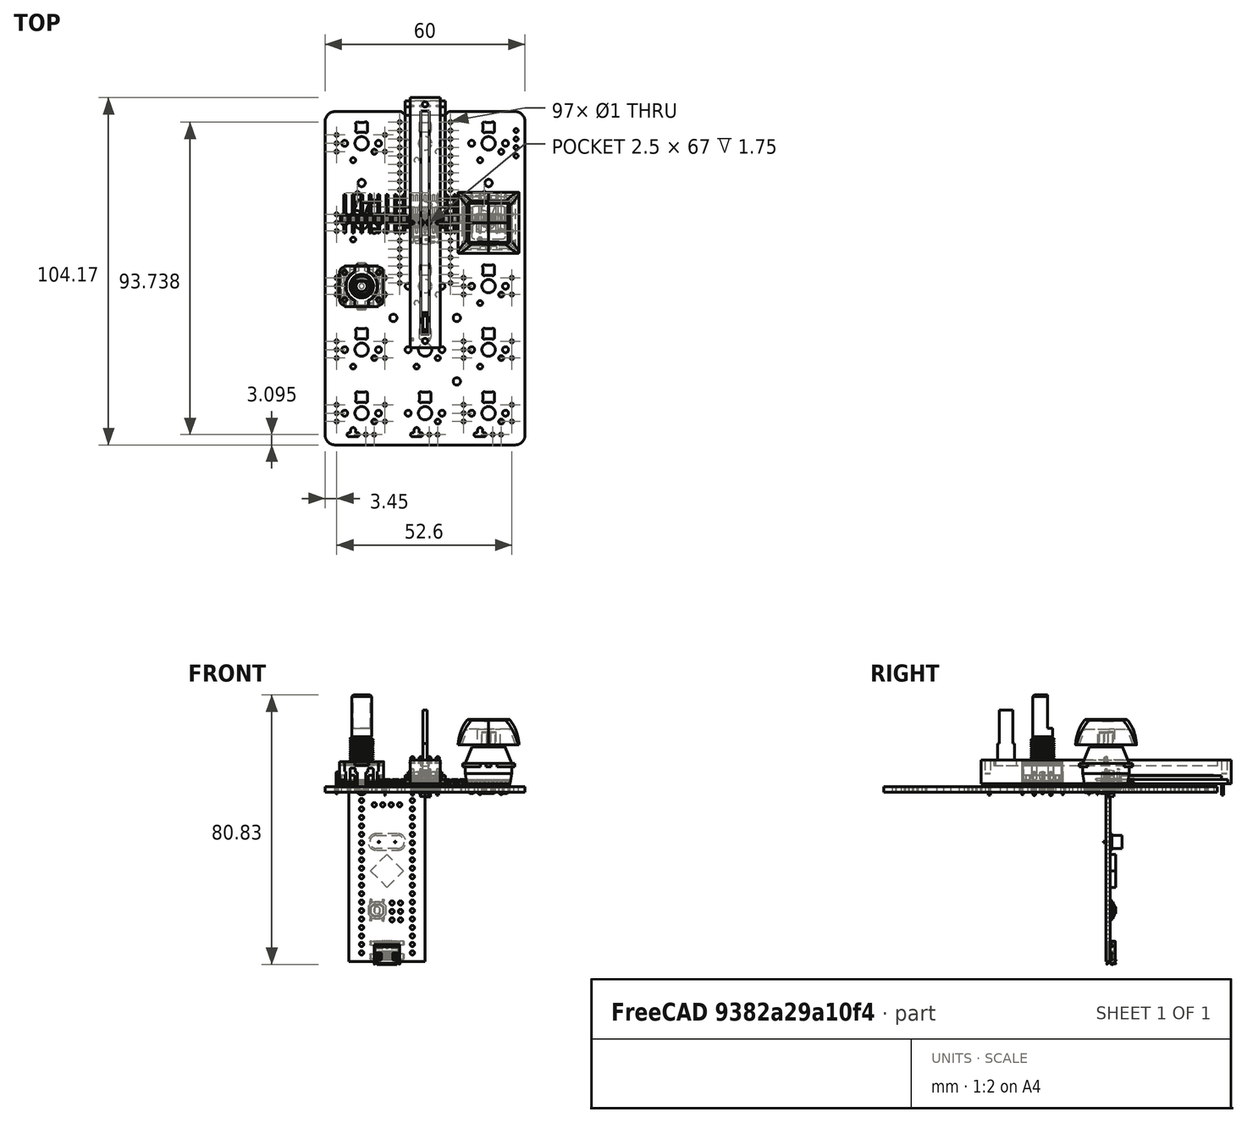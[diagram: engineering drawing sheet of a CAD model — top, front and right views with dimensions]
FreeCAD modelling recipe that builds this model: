
FCSTD DOCUMENT  (FreeCAD 2022.709R28846 (Git))
Label: keeby_cat_electronics_v1.0
License: All rights reserved
LicenseURL: http://en.wikipedia.org/wiki/All_rights_reserved
objects: Part::Feature×118, App::Link×53, Part::Compound2×10, App::Part×8, App::DocumentObjectGroup×3, PartDesign::CoordinateSystem×1, Sketcher::SketchObject×1
note: 120 computed .brp shape members not serialized (recipe doc carries the construction recipe); baked Part::Feature solids carry a one-line shape summary decoded from their .brp

FEATURE [PartDesign::CoordinateSystem] Local_CS_61fa
  AttacherType = Attacher::AttachEngine3D
  TreeRank = 3
FEATURE [Part::Feature] Pcb_61fa
  Placement = pos=(-92.16,90.4,-1) rot=(0,0,1;0rad)
  TreeRank = 4
  shape: bbox 60 x 100 x 1.6 mm, 469 faces (baked)
FEATURE [Sketcher::SketchObject] PCB_Sketch_61fa
  ArcFitTolerance = 0
  FullyConstrained = false
  TreeRank = 0
  sketch-geometry (16):
    g0: LineSegment StartX=-6.707 StartY=33.038 StartZ=0 EndX=-6.293 EndY=32.624 EndZ=0
    g1: LineSegment StartX=27 StartY=-66.669 StartZ=0 EndX=-27 EndY=-66.669 EndZ=0
    g2: LineSegment StartX=-27 StartY=33.331 StartZ=0 EndX=-7.414 EndY=33.331 EndZ=0
    g3: LineSegment StartX=-5.586 StartY=32.331 StartZ=0 EndX=5.586 EndY=32.331 EndZ=0
    g4: LineSegment StartX=7.414 StartY=33.331 StartZ=0 EndX=27 EndY=33.331 EndZ=0
    g5: LineSegment StartX=30 StartY=30.331 StartZ=0 EndX=30 EndY=-63.669 EndZ=0
    g6: LineSegment StartX=-30 StartY=-63.669 StartZ=0 EndX=-30 EndY=30.331 EndZ=0
    g7: LineSegment StartX=6.293 StartY=32.624 StartZ=0 EndX=6.707 EndY=33.038 EndZ=0
    g8: ArcOfCircle CenterX=-5.58541 CenterY=33.3319 CenterZ=0 NormalX=0 NormalY=0 NormalZ=-1 AngleXU=-1.57021 Radius=1.0009 StartAngle=0 EndAngle=0.784588
    g9: ArcOfCircle CenterX=-26.9989 CenterY=30.3299 CenterZ=0 NormalX=0 NormalY=0 NormalZ=-1 AngleXU=0.000364935 Radius=3.00109 StartAngle=6.28318 EndAngle=7.85325
    g10: ArcOfCircle CenterX=26.9989 CenterY=30.3299 CenterZ=0 NormalX=0 NormalY=0 NormalZ=-1 AngleXU=1.57116 Radius=3.00109 StartAngle=0 EndAngle=1.57007
    g11: ArcOfCircle CenterX=5.58549 CenterY=33.3317 CenterZ=0 NormalX=0 NormalY=0 NormalZ=-1 AngleXU=-2.35605 Radius=1.00072 StartAngle=0 EndAngle=0.784737
    g12: ArcOfCircle CenterX=-7.41449 CenterY=32.3303 CenterZ=0 NormalX=0 NormalY=0 NormalZ=-1 AngleXU=1.57129 Radius=1.00067 StartAngle=0 EndAngle=0.784782
    g13: ArcOfCircle CenterX=27.0006 CenterY=-63.6696 CenterZ=0 NormalX=0 NormalY=0 NormalZ=-1 AngleXU=3.14139 Radius=2.99938 StartAngle=0 EndAngle=1.57121
    g14: ArcOfCircle CenterX=7.4146 CenterY=32.3301 CenterZ=0 NormalX=0 NormalY=0 NormalZ=-1 AngleXU=0.785632 Radius=1.00093 StartAngle=0 EndAngle=0.784565
    g15: ArcOfCircle CenterX=-27.0006 CenterY=-63.6696 CenterZ=0 NormalX=0 NormalY=0 NormalZ=-1 AngleXU=-1.571 Radius=2.99938 StartAngle=0 EndAngle=1.57121
  constraints (16):
    c: Coincident(g6,g15)
    c: Coincident(g6,g9)
    c: Coincident(g1,g15)
    c: Coincident(g2,g9)
    c: Coincident(g2,g12)
    c: Coincident(g0,g12)
    c: Coincident(g0,g8)
    c: Coincident(g3,g8)
    c: Coincident(g3,g11)
    c: Coincident(g7,g11)
    c: Coincident(g7,g14)
    c: Coincident(g4,g14)
    c: Coincident(g1,g13)
    c: Coincident(g4,g10)
    c: Coincident(g5,g13)
    c: Coincident(g5,g10)
FEATURE [App::Part] Board_Geoms_61fa
  ClaimAllChildren = false
  ExportMode = 1
  Group = -> [Local_CS_61fa,Pcb_61fa,PCB_Sketch_61fa]
  Origin = -> Origin
  Placement = pos=(0,0,2) rot=(0,0,1;0rad)
  TreeRank = 5
  _ExportChildren = -> [Local_CS_61fa,Pcb_61fa,PCB_Sketch_61fa]
  _GroupVersion = 1
FEATURE [Part::Feature] Shape  label="EN4_PEC11-4220F-S0024_05183b338953"
  Placement = pos=(-19.05,-19.05,5.5) rot=(0.57735,0.57735,0.57735;2.0944rad)
  TreeRank = 0
  shape: bbox 14.93 x 14 x 30.2 mm, 452 faces (baked)
FEATURE [Part::Feature] Solid
  TreeRank = 0
  shape: bbox 3.202 x 2.804 x 1.782 mm, 91 faces (baked)
FEATURE [Part::Feature] Solid001
  TreeRank = 0
  shape: bbox 1.34 x 0.68 x 0.15 mm, 6 faces (baked)
FEATURE [Part::Feature] Solid002
  TreeRank = 0
  shape: bbox 1.34 x 0.68 x 0.15 mm, 7 faces (baked)
FEATURE [Part::Feature] Solid003
  TreeRank = 0
  shape: bbox 1.34 x 0.68 x 0.15 mm, 6 faces (baked)
FEATURE [Part::Feature] Solid004
  TreeRank = 0
  shape: bbox 1.34 x 0.68 x 0.15 mm, 6 faces (baked)
FEATURE [Part::Compound2] Compound  label="D11_LED_SK6812MINI-E v1_98239feeca95"
  Links = -> [Solid,Solid001,Solid002,Solid003,Solid004]
  Placement = pos=(-19.05,-19.33,0) rot=(0,0,1;3.14159rad)
  TreeRank = 0
FEATURE [App::Link] EN4_PEC11_4220F_S0024_05183b338953_ln_  label="EN3_PEC11-4220F-S0024_82a5f55121a7"
  AutoLinkLabel = false
  AutoPlacement = true
  LinkPlacement = pos=(19.05,0,5.5) rot=(0.57735,0.57735,0.57735;2.0944rad)
  LinkedObject = -> Shape
  Placement = pos=(19.05,0,5.5) rot=(0.57735,0.57735,0.57735;2.0944rad)
  ShowElement = false
  SyncGroupVisibility = false
  TreeRank = 0
  _LinkVersion = 1
FEATURE [Part::Feature] Shape001  label="SW4_cherry_mx v1_b31d9dcab5e3"
  Placement = pos=(19.05,0,0) rot=(0,0,1;3.14159rad)
  TreeRank = 0
  shape: bbox 15.6 x 16 x 18.5 mm, 105 faces (baked)
FEATURE [Part::Feature] Shape002  label="SW4_Keycap_adjusted v39_b31d9dcab5e3[2]"
  Placement = pos=(19.05,0,11.62) rot=(1,0,0;1.5708rad)
  TreeRank = 0
  shape: bbox 18.32 x 18.3 x 7.723 mm, 77 faces (baked)
FEATURE [App::Link] D11_LED_SK6812MINI_E_v1_98239feeca95_ln_  label="D15_LED_SK6812MINI-E v1_905db7f4c05a"
  AutoLinkLabel = false
  AutoPlacement = true
  LinkPlacement = pos=(19.05,23.5325,0) rot=(0,0,1;3.14159rad)
  LinkedObject = -> Compound
  Placement = pos=(19.05,23.5325,0) rot=(0,0,1;3.14159rad)
  ShowElement = false
  SyncGroupVisibility = false
  TreeRank = 0
  _LinkVersion = 1
FEATURE [App::Link] SW4_cherry_mx_v1_b31d9dcab5e3_ln_  label="SW13_cherry_mx v1_c6a9adc52cfe"
  AutoLinkLabel = false
  AutoPlacement = true
  LinkPlacement = pos=(19.05,-57.15,0) rot=(0,0,-1;3.14159rad)
  LinkedObject = -> Shape001
  Placement = pos=(19.05,-57.15,0) rot=(0,0,1;3.14159rad)
  ShowElement = false
  SyncGroupVisibility = false
  TreeRank = 0
  _LinkVersion = 1
FEATURE [App::Link] SW4_Keycap_adjusted_v39_b31d9dcab5e3_2__ln_  label="SW13_Keycap_adjusted v39_c6a9adc52cfe[2]"
  AutoLinkLabel = false
  AutoPlacement = true
  LinkPlacement = pos=(19.05,-57.15,11.55) rot=(1,0,0;1.5708rad)
  LinkedObject = -> Shape002
  Placement = pos=(19.05,-57.15,11.55) rot=(1,0,0;1.5708rad)
  ShowElement = false
  SyncGroupVisibility = false
  TreeRank = 0
  _LinkVersion = 1
FEATURE [App::Link] EN4_PEC11_4220F_S0024_05183b338953_ln_001  label="EN7_PEC11-4220F-S0024_a2e4a27f5c34"
  AutoLinkLabel = false
  AutoPlacement = true
  LinkPlacement = pos=(19.05,-38.1,5.5) rot=(0.57735,0.57735,0.57735;2.0944rad)
  LinkedObject = -> Shape
  Placement = pos=(19.05,-38.1,5.5) rot=(0.57735,0.57735,0.57735;2.0944rad)
  ShowElement = false
  SyncGroupVisibility = false
  TreeRank = 0
  _LinkVersion = 1
FEATURE [App::Link] D11_LED_SK6812MINI_E_v1_98239feeca95_ln_001  label="D3_LED_SK6812MINI-E v1_0005a27c16a8"
  AutoLinkLabel = false
  AutoPlacement = true
  LinkPlacement = pos=(19.05,-19.33,0) rot=(0,0,1;3.14159rad)
  LinkedObject = -> Compound
  Placement = pos=(19.05,-19.33,0) rot=(0,0,1;3.14159rad)
  ShowElement = false
  SyncGroupVisibility = false
  TreeRank = 0
  _LinkVersion = 1
FEATURE [App::Link] EN4_PEC11_4220F_S0024_05183b338953_ln_002  label="EN6_PEC11-4220F-S0024_fa3cd80f4dad"
  AutoLinkLabel = false
  AutoPlacement = true
  LinkPlacement = pos=(-19.05,-38.1,5.5) rot=(0.57735,0.57735,0.57735;2.0944rad)
  LinkedObject = -> Shape
  Placement = pos=(-19.05,-38.1,5.5) rot=(0.57735,0.57735,0.57735;2.0944rad)
  ShowElement = false
  SyncGroupVisibility = false
  TreeRank = 0
  _LinkVersion = 1
FEATURE [App::Link] D11_LED_SK6812MINI_E_v1_98239feeca95_ln_002  label="D7_LED_SK6812MINI-E v1_c4ce1cbe73e1"
  AutoLinkLabel = false
  AutoPlacement = true
  LinkPlacement = pos=(0,-38.38,0) rot=(0,0,1;3.14159rad)
  LinkedObject = -> Compound
  Placement = pos=(0,-38.38,0) rot=(0,0,1;3.14159rad)
  ShowElement = false
  SyncGroupVisibility = false
  TreeRank = 0
  _LinkVersion = 1
FEATURE [App::Link] EN4_PEC11_4220F_S0024_05183b338953_ln_003  label="EN8_PEC11-4220F-S0024_64c3b92ef519"
  AutoLinkLabel = false
  AutoPlacement = true
  LinkPlacement = pos=(-19.05,-57.15,5.5) rot=(0.57735,0.57735,0.57735;2.0944rad)
  LinkedObject = -> Shape
  Placement = pos=(-19.05,-57.15,5.5) rot=(0.57735,0.57735,0.57735;2.0944rad)
  ShowElement = false
  SyncGroupVisibility = false
  TreeRank = 0
  _LinkVersion = 1
FEATURE [App::Link] SW4_cherry_mx_v1_b31d9dcab5e3_ln_001  label="SW3_cherry_mx v1_a12fe743bfba"
  AutoLinkLabel = false
  AutoPlacement = true
  LinkPlacement = pos=(0,0,0) rot=(0,0,-1;3.14159rad)
  LinkedObject = -> Shape001
  Placement = pos=(0,0,0) rot=(0,0,1;3.14159rad)
  ShowElement = false
  SyncGroupVisibility = false
  TreeRank = 0
  _LinkVersion = 1
FEATURE [App::Link] SW4_Keycap_adjusted_v39_b31d9dcab5e3_2__ln_001  label="SW3_Keycap_adjusted v39_a12fe743bfba[2]"
  AutoLinkLabel = false
  AutoPlacement = true
  LinkPlacement = pos=(0,0,11.62) rot=(1,0,0;1.5708rad)
  LinkedObject = -> Shape002
  Placement = pos=(0,0,11.62) rot=(1,0,0;1.5708rad)
  ShowElement = false
  SyncGroupVisibility = false
  TreeRank = 0
  _LinkVersion = 1
FEATURE [App::Link] D11_LED_SK6812MINI_E_v1_98239feeca95_ln_003  label="D14_LED_SK6812MINI-E v1_1101d5bc822f"
  AutoLinkLabel = false
  AutoPlacement = true
  LinkPlacement = pos=(0,23.5325,0) rot=(0,0,1;3.14159rad)
  LinkedObject = -> Compound
  Placement = pos=(0,23.5325,0) rot=(0,0,1;3.14159rad)
  ShowElement = false
  SyncGroupVisibility = false
  TreeRank = 0
  _LinkVersion = 1
FEATURE [App::Link] EN4_PEC11_4220F_S0024_05183b338953_ln_004  label="EN9_PEC11-4220F-S0024_1bcb47a43990"
  AutoLinkLabel = false
  AutoPlacement = true
  LinkPlacement = pos=(19.05,-57.15,5.5) rot=(0.57735,0.57735,0.57735;2.0944rad)
  LinkedObject = -> Shape
  Placement = pos=(19.05,-57.15,5.5) rot=(0.57735,0.57735,0.57735;2.0944rad)
  ShowElement = false
  SyncGroupVisibility = false
  TreeRank = 0
  _LinkVersion = 1
FEATURE [App::Link] SW4_cherry_mx_v1_b31d9dcab5e3_ln_002  label="SW14_cherry_mx v1_3f50532e5e34"
  AutoLinkLabel = false
  AutoPlacement = true
  LinkPlacement = pos=(0,23.8125,0) rot=(0,0,-1;3.14159rad)
  LinkedObject = -> Shape001
  Placement = pos=(0,23.8125,0) rot=(0,0,1;3.14159rad)
  ShowElement = false
  SyncGroupVisibility = false
  TreeRank = 0
  _LinkVersion = 1
FEATURE [App::Link] SW4_Keycap_adjusted_v39_b31d9dcab5e3_2__ln_002  label="SW14_Keycap_adjusted v39_3f50532e5e34[2]"
  AutoLinkLabel = false
  AutoPlacement = true
  LinkPlacement = pos=(0,23.8125,11.62) rot=(1,0,0;1.5708rad)
  LinkedObject = -> Shape002
  Placement = pos=(0,23.8125,11.62) rot=(1,0,0;1.5708rad)
  ShowElement = false
  SyncGroupVisibility = false
  TreeRank = 0
  _LinkVersion = 1
FEATURE [Part::Feature] Solid005
  TreeRank = 0
  shape: bbox 10.16 x 2.5 x 3.5 mm, 38 faces (baked)
FEATURE [Part::Feature] Solid006 .. Solid009  x4 (patterned run collapsed; names and placements below)
  TreeRank = 0
  shape: bbox 1.22 x 1.12 x 5.697 mm, 20 faces (baked)
FEATURE [Part::Compound2] Compound001  label="Pin Socket 1x4 v1"
  Links = -> [Solid005,Solid006,Solid007,Solid008,Solid009]
  TreeRank = 0
FEATURE [Part::Feature] Solid010
  TreeRank = 0
  shape: bbox 10.12 x 2.5 x 1.5 mm, 34 faces (baked)
FEATURE [Part::Feature] Solid011 .. Solid014  x4 (patterned run collapsed; names and placements below)
  TreeRank = 0
  shape: bbox 0.64 x 0.64 x 7.5 mm, 14 faces (baked)
FEATURE [Part::Compound2] Compound002  label="Pin Header 1.4 v1"
  Links = -> [Solid010,Solid011,Solid012,Solid013,Solid014]
  Placement = pos=(0,0,3.5) rot=(0,0,1;0rad)
  TreeRank = 0
FEATURE [Part::Feature] Solid015
  TreeRank = 0
  shape: bbox 12.05 x 37.95 x 1.2 mm, 13 faces (baked)
FEATURE [Part::Feature] Solid016
  TreeRank = 0
  shape: bbox 1.9 x 1.9 x 1.2 mm, 4 faces (baked)
FEATURE [Part::Feature] Solid017
  TreeRank = 0
  shape: bbox 1.9 x 1.9 x 1.2 mm, 4 faces (baked)
FEATURE [Part::Feature] Solid018
  TreeRank = 0
  shape: bbox 1.9 x 1.9 x 1.2 mm, 4 faces (baked)
FEATURE [Part::Feature] Solid019
  TreeRank = 0
  shape: bbox 1.9 x 1.9 x 1.2 mm, 7 faces (baked)
FEATURE [Part::Feature] Solid020
  TreeRank = 0
  shape: bbox 12.05 x 30.1 x 1.2 mm, 6 faces (baked)
FEATURE [Part::Feature] Solid021
  TreeRank = 0
  shape: bbox 11.87 x 27.54 x 0.1 mm, 6 faces (baked)
FEATURE [Part::Feature] Solid022
  TreeRank = 0
  shape: bbox 0.5698 x 0.7402 x 0.01 mm, 37 faces (baked)
FEATURE [Part::Feature] Solid023
  TreeRank = 0
  shape: bbox 0.6328 x 0.7402 x 0.01 mm, 24 faces (baked)
FEATURE [Part::Feature] Solid024
  TreeRank = 0
  shape: bbox 0.564 x 0.7158 x 0.01 mm, 12 faces (baked)
FEATURE [Part::Feature] Solid025
  TreeRank = 0
  shape: bbox 0.5918 x 0.7158 x 0.01 mm, 24 faces (baked)
FEATURE [Part::Feature] Solid026
  TreeRank = 0
  shape: bbox 0.5698 x 0.7402 x 0.01 mm, 37 faces (baked)
FEATURE [Part::Feature] Solid027
  TreeRank = 0
  shape: bbox 0.5918 x 0.7158 x 0.01 mm, 24 faces (baked)
FEATURE [Part::Feature] Solid028
  TreeRank = 0
  shape: bbox 0.5918 x 0.7158 x 0.01 mm, 14 faces (baked)
FEATURE [Part::Feature] Solid029
  TreeRank = 0
  shape: bbox 0.6328 x 0.7402 x 0.01 mm, 24 faces (baked)
FEATURE [Part::Feature] Solid030
  TreeRank = 0
  shape: bbox 0.6621 x 0.7402 x 0.01 mm, 31 faces (baked)
FEATURE [Part::Feature] Solid031
  TreeRank = 0
  shape: bbox 0.6548 x 0.7158 x 0.01 mm, 11 faces (baked)
FEATURE [Part::Feature] Solid032
  TreeRank = 0
  shape: bbox 0.6328 x 0.7402 x 0.01 mm, 24 faces (baked)
FEATURE [Part::Feature] Solid033
  TreeRank = 0
  shape: bbox 0.6699 x 0.7158 x 0.01 mm, 15 faces (baked)
FEATURE [Part::Compound2] Compound003  label="OLED Module v2"
  Links = -> [Solid015,Solid016,Solid017,Solid018,Solid019,Solid020,Solid021,Solid022,Solid023,Solid024,Solid025,Solid026,Solid027,Solid028,Solid029,Solid030,Solid031,Solid032,Solid033]
  Placement = pos=(0,0,5) rot=(0,0,1;0rad)
  TreeRank = 0
FEATURE [Part::Feature] Solid034 .. Solid037  x4 (patterned run collapsed; names and placements below)
  TreeRank = 0
  shape: bbox 1.781 x 1.781 x 1.906 mm, 6 faces (baked)
FEATURE [Part::Compound2] Compound004
  Links = -> [Solid034,Solid035,Solid036,Solid037]
  TreeRank = 0
FEATURE [App::Part] Part  label="OL1_OLED Module with Pins v1_e05ba27373dd"
  ClaimAllChildren = false
  ExportMode = 1
  Group = -> [Compound001,Compound002,Compound003,Compound004,Solid009,Solid005,Solid007,Solid006,Solid008,Solid010,Solid011,Solid013,Solid012,Solid014,Solid017,Solid019,Solid022,Solid015,Solid016,Solid018,Solid020,Solid021,Solid023,Solid033,Solid030,Solid027,Solid032,Solid025,Solid029,Solid026,Solid024,Solid028,Solid031,Solid037,Solid035,Solid036,Solid034]
  Origin = -> Origin008
  Placement = pos=(27.305,23.8125,0) rot=(0,0,1;1.5708rad)
  TreeRank = 0
  _ExportChildren = -> [Compound001,Compound002,Compound003,Compound004]
  _GroupVersion = 1
FEATURE [App::Link] D11_LED_SK6812MINI_E_v1_98239feeca95_ln_004  label="D2_LED_SK6812MINI-E v1_07ac1b52877c"
  AutoLinkLabel = false
  AutoPlacement = true
  LinkPlacement = pos=(19.05,-38.38,0) rot=(0,0,1;3.14159rad)
  LinkedObject = -> Compound
  Placement = pos=(19.05,-38.38,0) rot=(0,0,1;3.14159rad)
  ShowElement = false
  SyncGroupVisibility = false
  TreeRank = 0
  _LinkVersion = 1
FEATURE [App::Link] D11_LED_SK6812MINI_E_v1_98239feeca95_ln_005  label="D6_LED_SK6812MINI-E v1_10a1c9ba8b18"
  AutoLinkLabel = false
  AutoPlacement = true
  LinkPlacement = pos=(0,-19.33,0) rot=(0,0,1;3.14159rad)
  LinkedObject = -> Compound
  Placement = pos=(0,-19.33,0) rot=(0,0,1;3.14159rad)
  ShowElement = false
  SyncGroupVisibility = false
  TreeRank = 0
  _LinkVersion = 1
FEATURE [App::Link] D11_LED_SK6812MINI_E_v1_98239feeca95_ln_006  label="D8_LED_SK6812MINI-E v1_ec62b56ff335"
  AutoLinkLabel = false
  AutoPlacement = true
  LinkPlacement = pos=(0,-57.43,0) rot=(0,0,1;3.14159rad)
  LinkedObject = -> Compound
  Placement = pos=(0,-57.43,0) rot=(0,0,1;3.14159rad)
  ShowElement = false
  SyncGroupVisibility = false
  TreeRank = 0
  _LinkVersion = 1
FEATURE [App::Link] D11_LED_SK6812MINI_E_v1_98239feeca95_ln_007  label="D13_LED_SK6812MINI-E v1_c8149a755eaa"
  AutoLinkLabel = false
  AutoPlacement = true
  LinkPlacement = pos=(-19.05,23.5325,0) rot=(0,0,1;3.14159rad)
  LinkedObject = -> Compound
  Placement = pos=(-19.05,23.5325,0) rot=(0,0,1;3.14159rad)
  ShowElement = false
  SyncGroupVisibility = false
  TreeRank = 0
  _LinkVersion = 1
FEATURE [App::Link] SW4_cherry_mx_v1_b31d9dcab5e3_ln_003  label="SW9_cherry_mx v1_ef7394e8c103"
  AutoLinkLabel = false
  AutoPlacement = true
  LinkPlacement = pos=(0,-38.1,0) rot=(0,0,-1;3.14159rad)
  LinkedObject = -> Shape001
  Placement = pos=(0,-38.1,0) rot=(0,0,1;3.14159rad)
  ShowElement = false
  SyncGroupVisibility = false
  TreeRank = 0
  _LinkVersion = 1
FEATURE [App::Link] SW4_Keycap_adjusted_v39_b31d9dcab5e3_2__ln_003  label="SW9_Keycap_adjusted v39_ef7394e8c103[2]"
  AutoLinkLabel = false
  AutoPlacement = true
  LinkPlacement = pos=(0,-38.1,11.62) rot=(1,0,0;1.5708rad)
  LinkedObject = -> Shape002
  Placement = pos=(0,-38.1,11.62) rot=(1,0,0;1.5708rad)
  ShowElement = false
  SyncGroupVisibility = false
  TreeRank = 0
  _LinkVersion = 1
FEATURE [App::Link] EN4_PEC11_4220F_S0024_05183b338953_ln_005  label="EN1_PEC11-4220F-S0024_84fb90879178"
  AutoLinkLabel = false
  AutoPlacement = true
  LinkPlacement = pos=(-19.05,23.8125,5.5) rot=(0.57735,0.57735,0.57735;2.0944rad)
  LinkedObject = -> Shape
  Placement = pos=(-19.05,23.8125,5.5) rot=(0.57735,0.57735,0.57735;2.0944rad)
  ShowElement = false
  SyncGroupVisibility = false
  TreeRank = 0
  _LinkVersion = 1
FEATURE [App::Link] D11_LED_SK6812MINI_E_v1_98239feeca95_ln_008  label="D1_LED_SK6812MINI-E v1_b059c628641d"
  AutoLinkLabel = false
  AutoPlacement = true
  LinkPlacement = pos=(19.05,-57.43,0) rot=(0,0,1;3.14159rad)
  LinkedObject = -> Compound
  Placement = pos=(19.05,-57.43,0) rot=(0,0,1;3.14159rad)
  ShowElement = false
  SyncGroupVisibility = false
  TreeRank = 0
  _LinkVersion = 1
FEATURE [App::Link] SW4_cherry_mx_v1_b31d9dcab5e3_ln_004  label="SW11_cherry_mx v1_2edbdd72f56d"
  AutoLinkLabel = false
  AutoPlacement = true
  LinkPlacement = pos=(-19.05,-57.15,0) rot=(0,0,-1;3.14159rad)
  LinkedObject = -> Shape001
  Placement = pos=(-19.05,-57.15,0) rot=(0,0,1;3.14159rad)
  ShowElement = false
  SyncGroupVisibility = false
  TreeRank = 0
  _LinkVersion = 1
FEATURE [App::Link] SW4_Keycap_adjusted_v39_b31d9dcab5e3_2__ln_004  label="SW11_Keycap_adjusted v39_2edbdd72f56d[2]"
  AutoLinkLabel = false
  AutoPlacement = true
  LinkPlacement = pos=(-19.05,-57.15,11.55) rot=(1,0,0;1.5708rad)
  LinkedObject = -> Shape002
  Placement = pos=(-19.05,-57.15,11.55) rot=(1,0,0;1.5708rad)
  ShowElement = false
  SyncGroupVisibility = false
  TreeRank = 0
  _LinkVersion = 1
FEATURE [App::Link] SW4_cherry_mx_v1_b31d9dcab5e3_ln_005  label="SW15_cherry_mx v1_affe07005f5e"
  AutoLinkLabel = false
  AutoPlacement = true
  LinkPlacement = pos=(19.05,23.8125,0) rot=(0,0,-1;3.14159rad)
  LinkedObject = -> Shape001
  Placement = pos=(19.05,23.8125,0) rot=(0,0,1;3.14159rad)
  ShowElement = false
  SyncGroupVisibility = false
  TreeRank = 0
  _LinkVersion = 1
FEATURE [App::Link] SW4_Keycap_adjusted_v39_b31d9dcab5e3_2__ln_005  label="SW15_Keycap_adjusted v39_affe07005f5e[2]"
  AutoLinkLabel = false
  AutoPlacement = true
  LinkPlacement = pos=(19.05,23.8125,11.62) rot=(1,0,0;1.5708rad)
  LinkedObject = -> Shape002
  Placement = pos=(19.05,23.8125,11.62) rot=(1,0,0;1.5708rad)
  ShowElement = false
  SyncGroupVisibility = false
  TreeRank = 0
  _LinkVersion = 1
FEATURE [Part::Feature] Solid038  label="slider"
  TreeRank = 0
  shape: bbox 2 x 6 x 16.75 mm, 15 faces (baked)
FEATURE [Part::Feature] Solid039  label="base"
  TreeRank = 0
  shape: bbox 9 x 75 x 7 mm, 15 faces (baked)
FEATURE [Part::Feature] Solid040 .. Solid045  x6 (patterned run collapsed; names and placements below)
  TreeRank = 0
  shape: bbox 0.6 x 0.6 x 3.5 mm, 6 faces (baked)
FEATURE [Part::Compound2] Compound005  label="leads"
  Links = -> [Solid040,Solid041,Solid042,Solid043,Solid044,Solid045]
  TreeRank = 0
FEATURE [App::Part] Part001  label="VR3_B10K B103 sliding potentiometer v8_0e7ca3619782"
  ClaimAllChildren = false
  ExportMode = 1
  Group = -> [Solid038,Solid039,Compound005,Solid045,Solid042,Solid043,Solid044,Solid041,Solid040]
  Origin = -> Origin009
  Placement = pos=(19.05,-28.575,0) rot=(0,0,1;3.14159rad)
  TreeRank = 0
  _ExportChildren = -> [Solid038,Solid039,Compound005]
  _GroupVersion = 1
FEATURE [App::Link] D11_LED_SK6812MINI_E_v1_98239feeca95_ln_009  label="D12_LED_SK6812MINI-E v1_20bb1948b82e"
  AutoLinkLabel = false
  AutoPlacement = true
  LinkPlacement = pos=(-20.8,0.05,0) rot=(0,0,1;2.79253rad)
  LinkedObject = -> Compound
  Placement = pos=(-20.8,0.05,0) rot=(0,0,1;2.79253rad)
  ShowElement = false
  SyncGroupVisibility = false
  TreeRank = 0
  _LinkVersion = 1
FEATURE [App::Link] D11_LED_SK6812MINI_E_v1_98239feeca95_ln_010  label="D9_LED_SK6812MINI-E v1_28ac90cb7290"
  AutoLinkLabel = false
  AutoPlacement = true
  LinkPlacement = pos=(-19.05,-57.43,0) rot=(0,0,1;3.14159rad)
  LinkedObject = -> Compound
  Placement = pos=(-19.05,-57.43,0) rot=(0,0,1;3.14159rad)
  ShowElement = false
  SyncGroupVisibility = false
  TreeRank = 0
  _LinkVersion = 1
FEATURE [App::Link] SW4_cherry_mx_v1_b31d9dcab5e3_ln_006  label="SW8_cherry_mx v1_d46a69a4d81d"
  AutoLinkLabel = false
  AutoPlacement = true
  LinkPlacement = pos=(-19.05,-38.1,0) rot=(0,0,-1;3.14159rad)
  LinkedObject = -> Shape001
  Placement = pos=(-19.05,-38.1,0) rot=(0,0,1;3.14159rad)
  ShowElement = false
  SyncGroupVisibility = false
  TreeRank = 0
  _LinkVersion = 1
FEATURE [App::Link] SW4_Keycap_adjusted_v39_b31d9dcab5e3_2__ln_006  label="SW8_Keycap_adjusted v39_d46a69a4d81d[2]"
  AutoLinkLabel = false
  AutoPlacement = true
  LinkPlacement = pos=(-19.05,-38.1,11.62) rot=(1,0,0;1.5708rad)
  LinkedObject = -> Shape002
  Placement = pos=(-19.05,-38.1,11.62) rot=(1,0,0;1.5708rad)
  ShowElement = false
  SyncGroupVisibility = false
  TreeRank = 0
  _LinkVersion = 1
FEATURE [App::Link] EN4_PEC11_4220F_S0024_05183b338953_ln_006  label="EN5_PEC11-4220F-S0024_9304346049a0"
  AutoLinkLabel = false
  AutoPlacement = true
  LinkPlacement = pos=(19.05,-19.05,5.5) rot=(0.57735,0.57735,0.57735;2.0944rad)
  LinkedObject = -> Shape
  Placement = pos=(19.05,-19.05,5.5) rot=(0.57735,0.57735,0.57735;2.0944rad)
  ShowElement = false
  SyncGroupVisibility = false
  TreeRank = 0
  _LinkVersion = 1
FEATURE [App::Link] SW4_cherry_mx_v1_b31d9dcab5e3_ln_007  label="SW12_cherry_mx v1_0fc034a3f74b"
  AutoLinkLabel = false
  AutoPlacement = true
  LinkPlacement = pos=(0,-57.15,0) rot=(0,0,-1;3.14159rad)
  LinkedObject = -> Shape001
  Placement = pos=(0,-57.15,0) rot=(0,0,1;3.14159rad)
  ShowElement = false
  SyncGroupVisibility = false
  TreeRank = 0
  _LinkVersion = 1
FEATURE [App::Link] SW4_Keycap_adjusted_v39_b31d9dcab5e3_2__ln_007  label="SW12_Keycap_adjusted v39_0fc034a3f74b[2]"
  AutoLinkLabel = false
  AutoPlacement = true
  LinkPlacement = pos=(0,-57.15,11.55) rot=(1,0,0;1.5708rad)
  LinkedObject = -> Shape002
  Placement = pos=(0,-57.15,11.55) rot=(1,0,0;1.5708rad)
  ShowElement = false
  SyncGroupVisibility = false
  TreeRank = 0
  _LinkVersion = 1
FEATURE [App::Link] VR3_B10K_B103_sliding_potentiometer_v8_0e7ca3619782_ln_  label="VR1_B10K B103 sliding potentiometer v8_28896c78a179"
  AutoLinkLabel = false
  AutoPlacement = true
  LinkPlacement = pos=(-19.05,-28.575,0) rot=(0,0,1;3.14159rad)
  LinkedObject = -> Part001
  Placement = pos=(-19.05,-28.575,0) rot=(0,0,1;3.14159rad)
  ShowElement = false
  SyncGroupVisibility = false
  TreeRank = 0
  _LinkVersion = 1
FEATURE [App::Link] D11_LED_SK6812MINI_E_v1_98239feeca95_ln_011  label="D10_LED_SK6812MINI-E v1_e4e8fa4bb40b"
  AutoLinkLabel = false
  AutoPlacement = true
  LinkPlacement = pos=(-19.05,-38.38,0) rot=(0,0,1;3.14159rad)
  LinkedObject = -> Compound
  Placement = pos=(-19.05,-38.38,0) rot=(0,0,1;3.14159rad)
  ShowElement = false
  SyncGroupVisibility = false
  TreeRank = 0
  _LinkVersion = 1
FEATURE [App::Link] SW4_cherry_mx_v1_b31d9dcab5e3_ln_008  label="SW7_cherry_mx v1_eab81a92fce9"
  AutoLinkLabel = false
  AutoPlacement = true
  LinkPlacement = pos=(19.05,-19.05,0) rot=(0,0,-1;3.14159rad)
  LinkedObject = -> Shape001
  Placement = pos=(19.05,-19.05,0) rot=(0,0,1;3.14159rad)
  ShowElement = false
  SyncGroupVisibility = false
  TreeRank = 0
  _LinkVersion = 1
FEATURE [App::Link] SW4_Keycap_adjusted_v39_b31d9dcab5e3_2__ln_008  label="SW7_Keycap_adjusted v39_eab81a92fce9[2]"
  AutoLinkLabel = false
  AutoPlacement = true
  LinkPlacement = pos=(19.05,-19.05,11.62) rot=(1,0,0;1.5708rad)
  LinkedObject = -> Shape002
  Placement = pos=(19.05,-19.05,11.62) rot=(1,0,0;1.5708rad)
  ShowElement = false
  SyncGroupVisibility = false
  TreeRank = 0
  _LinkVersion = 1
FEATURE [App::Link] SW4_cherry_mx_v1_b31d9dcab5e3_ln_009  label="SW6_cherry_mx v1_99d446687b03"
  AutoLinkLabel = false
  AutoPlacement = true
  LinkPlacement = pos=(0,-19.05,0) rot=(0,0,-1;3.14159rad)
  LinkedObject = -> Shape001
  Placement = pos=(0,-19.05,0) rot=(0,0,1;3.14159rad)
  ShowElement = false
  SyncGroupVisibility = false
  TreeRank = 0
  _LinkVersion = 1
FEATURE [App::Link] SW4_Keycap_adjusted_v39_b31d9dcab5e3_2__ln_009  label="SW6_Keycap_adjusted v39_99d446687b03[2]"
  AutoLinkLabel = false
  AutoPlacement = true
  LinkPlacement = pos=(0,-19.05,11.62) rot=(1,0,0;1.5708rad)
  LinkedObject = -> Shape002
  Placement = pos=(0,-19.05,11.62) rot=(1,0,0;1.5708rad)
  ShowElement = false
  SyncGroupVisibility = false
  TreeRank = 0
  _LinkVersion = 1
FEATURE [App::Link] SW4_cherry_mx_v1_b31d9dcab5e3_ln_010  label="SW10_cherry_mx v1_ca0f646de897"
  AutoLinkLabel = false
  AutoPlacement = true
  LinkPlacement = pos=(19.05,-38.1,0) rot=(0,0,-1;3.14159rad)
  LinkedObject = -> Shape001
  Placement = pos=(19.05,-38.1,0) rot=(0,0,1;3.14159rad)
  ShowElement = false
  SyncGroupVisibility = false
  TreeRank = 0
  _LinkVersion = 1
FEATURE [App::Link] SW4_Keycap_adjusted_v39_b31d9dcab5e3_2__ln_010  label="SW10_Keycap_adjusted v39_ca0f646de897[2]"
  AutoLinkLabel = false
  AutoPlacement = true
  LinkPlacement = pos=(19.05,-38.1,11.62) rot=(1,0,0;1.5708rad)
  LinkedObject = -> Shape002
  Placement = pos=(19.05,-38.1,11.62) rot=(1,0,0;1.5708rad)
  ShowElement = false
  SyncGroupVisibility = false
  TreeRank = 0
  _LinkVersion = 1
FEATURE [App::Link] EN4_PEC11_4220F_S0024_05183b338953_ln_007  label="EN2_PEC11-4220F-S0024_265aca994ef9"
  AutoLinkLabel = false
  AutoPlacement = true
  LinkPlacement = pos=(-19.05,0,5.5) rot=(0.57735,0.57735,0.57735;2.0944rad)
  LinkedObject = -> Shape
  Placement = pos=(-19.05,0,5.5) rot=(0.57735,0.57735,0.57735;2.0944rad)
  ShowElement = false
  SyncGroupVisibility = false
  TreeRank = 0
  _LinkVersion = 1
FEATURE [App::Link] D11_LED_SK6812MINI_E_v1_98239feeca95_ln_012  label="D4_LED_SK6812MINI-E v1_6e3c03ec8126"
  AutoLinkLabel = false
  AutoPlacement = true
  LinkPlacement = pos=(17.3,0.05,0) rot=(0,0,1;2.79253rad)
  LinkedObject = -> Compound
  Placement = pos=(17.3,0.05,0) rot=(0,0,1;2.79253rad)
  ShowElement = false
  SyncGroupVisibility = false
  TreeRank = 0
  _LinkVersion = 1
FEATURE [App::Link] D11_LED_SK6812MINI_E_v1_98239feeca95_ln_013  label="D5_LED_SK6812MINI-E v1_dc6b6f9343d5"
  AutoLinkLabel = false
  AutoPlacement = true
  LinkPlacement = pos=(-1.75,0.05,0) rot=(0,0,1;2.79253rad)
  LinkedObject = -> Compound
  Placement = pos=(-1.75,0.05,0) rot=(0,0,1;2.79253rad)
  ShowElement = false
  SyncGroupVisibility = false
  TreeRank = 0
  _LinkVersion = 1
FEATURE [App::Link] VR3_B10K_B103_sliding_potentiometer_v8_0e7ca3619782_ln_001  label="VR2_B10K B103 sliding potentiometer v8_2f7c46c00bb4"
  AutoLinkLabel = false
  AutoPlacement = true
  LinkPlacement = pos=(0,-28.575,0) rot=(0,0,1;3.14159rad)
  LinkedObject = -> Part001
  Placement = pos=(0,-28.575,0) rot=(0,0,1;3.14159rad)
  ShowElement = false
  SyncGroupVisibility = false
  TreeRank = 0
  _LinkVersion = 1
FEATURE [App::Link] SW4_cherry_mx_v1_b31d9dcab5e3_ln_011  label="SW5_cherry_mx v1_2b04c5b0159e"
  AutoLinkLabel = false
  AutoPlacement = true
  LinkPlacement = pos=(-19.05,-19.05,0) rot=(0,0,-1;3.14159rad)
  LinkedObject = -> Shape001
  Placement = pos=(-19.05,-19.05,0) rot=(0,0,1;3.14159rad)
  ShowElement = false
  SyncGroupVisibility = false
  TreeRank = 0
  _LinkVersion = 1
FEATURE [App::Link] SW4_Keycap_adjusted_v39_b31d9dcab5e3_2__ln_011  label="SW5_Keycap_adjusted v39_2b04c5b0159e[2]"
  AutoLinkLabel = false
  AutoPlacement = true
  LinkPlacement = pos=(-19.05,-19.05,11.62) rot=(1,0,0;1.5708rad)
  LinkedObject = -> Shape002
  Placement = pos=(-19.05,-19.05,11.62) rot=(1,0,0;1.5708rad)
  ShowElement = false
  SyncGroupVisibility = false
  TreeRank = 0
  _LinkVersion = 1
FEATURE [App::Link] SW4_cherry_mx_v1_b31d9dcab5e3_ln_012  label="SW2_cherry_mx v1_ece5ddd5dac5"
  AutoLinkLabel = false
  AutoPlacement = true
  LinkPlacement = pos=(-19.05,0,0) rot=(0,0,-1;3.14159rad)
  LinkedObject = -> Shape001
  Placement = pos=(-19.05,0,0) rot=(0,0,1;3.14159rad)
  ShowElement = false
  SyncGroupVisibility = false
  TreeRank = 0
  _LinkVersion = 1
FEATURE [App::Link] SW4_Keycap_adjusted_v39_b31d9dcab5e3_2__ln_012  label="SW2_Keycap_adjusted v39_ece5ddd5dac5[2]"
  AutoLinkLabel = false
  AutoPlacement = true
  LinkPlacement = pos=(-19.05,0,11.62) rot=(1,0,0;1.5708rad)
  LinkedObject = -> Shape002
  Placement = pos=(-19.05,0,11.62) rot=(1,0,0;1.5708rad)
  ShowElement = false
  SyncGroupVisibility = false
  TreeRank = 0
  _LinkVersion = 1
FEATURE [App::Link] SW4_cherry_mx_v1_b31d9dcab5e3_ln_013  label="SW1_cherry_mx v1_79efe81ded34"
  AutoLinkLabel = false
  AutoPlacement = true
  LinkPlacement = pos=(-19.05,23.8125,0) rot=(0,0,-1;3.14159rad)
  LinkedObject = -> Shape001
  Placement = pos=(-19.05,23.8125,0) rot=(0,0,1;3.14159rad)
  ShowElement = false
  SyncGroupVisibility = false
  TreeRank = 0
  _LinkVersion = 1
FEATURE [App::Link] SW4_Keycap_adjusted_v39_b31d9dcab5e3_2__ln_013  label="SW1_Keycap_adjusted v39_79efe81ded34[2]"
  AutoLinkLabel = false
  AutoPlacement = true
  LinkPlacement = pos=(-19.05,23.8125,11.62) rot=(1,0,0;1.5708rad)
  LinkedObject = -> Shape002
  Placement = pos=(-19.05,23.8125,11.62) rot=(1,0,0;1.5708rad)
  ShowElement = false
  SyncGroupVisibility = false
  TreeRank = 0
  _LinkVersion = 1
FEATURE [Part::Feature] Solid046  label="Oscillator_HC-49/S v1"
  Placement = pos=(-11.43,1.27,-17.526) rot=(0,1,0;1.5708rad)
  TreeRank = 0
  shape: bbox 11.35 x 5.5 x 5 mm, 15 faces (baked)
FEATURE [Part::Feature] Solid047  label="STM32F103C8T6_BluePill_Board v6"
  TreeRank = 0
  shape: bbox 22.86 x 1.27 x 53.34 mm, 60 faces (baked)
FEATURE [Part::Feature] Solid048
  TreeRank = 0
  shape: bbox 3.2 x 2.38 x 8 mm, 30 faces (baked)
FEATURE [Part::Feature] Solid049
  TreeRank = 0
  shape: bbox 3.8 x 1.01 x 0.5 mm, 18 faces (baked)
FEATURE [Part::Feature] Solid050
  TreeRank = 0
  shape: bbox 3.8 x 1.01 x 0.5 mm, 18 faces (baked)
FEATURE [Part::Compound2] Compound006  label="Oscillator_MC-306 v3"
  Links = -> [Solid048,Solid049,Solid050]
  Placement = pos=(-11.43,1.43,-12.192) rot=(0,-1,0;1.5708rad)
  TreeRank = 0
FEATURE [Part::Feature] Solid051  label="STM32_LQFP48 v3"
  Placement = pos=(-11.43,1.27,-26.162) rot=(0,1,0;0.785398rad)
  TreeRank = 0
  shape: bbox 9.899 x 1.6 x 9.899 mm, 6 faces (baked)
FEATURE [Part::Feature] Solid052  label="Tactile_SMD_5x5mm v1"
  Placement = pos=(-14.43,1.3192,-38) rot=(0.57735,0.57735,0.57735;4.18879rad)
  TreeRank = 0
  shape: bbox 5.081 x 1.525 x 6.501 mm, 70 faces (baked)
FEATURE [Part::Feature] Solid053  label="micro_usb_socket v1"
  Placement = pos=(-11.43,1.535,-53.8) rot=(0,1,0;3.14159rad)
  TreeRank = 0
  shape: bbox 10.2 x 2.83 x 7.23 mm, 434 faces (baked)
FEATURE [Part::Feature] Solid054
  TreeRank = 0
  shape: bbox 2.54 x 2.5 x 2.54 mm, 26 faces (baked)
FEATURE [Part::Feature] Solid055
  TreeRank = 0
  shape: bbox 0.64 x 10 x 4.8 mm, 18 faces (baked)
FEATURE [Part::Feature] Solid056
  TreeRank = 0
  shape: bbox 2.54 x 2.5 x 2.54 mm, 26 faces (baked)
FEATURE [Part::Feature] Solid057
  TreeRank = 0
  shape: bbox 2.54 x 2.5 x 2.54 mm, 26 faces (baked)
FEATURE [Part::Feature] Solid058
  TreeRank = 0
  shape: bbox 2.54 x 2.5 x 2.54 mm, 26 faces (baked)
FEATURE [Part::Feature] Solid059
  TreeRank = 0
  shape: bbox 0.64 x 10 x 4.8 mm, 18 faces (baked)
FEATURE [Part::Feature] Solid060
  TreeRank = 0
  shape: bbox 0.64 x 10 x 4.8 mm, 18 faces (baked)
FEATURE [Part::Feature] Solid061
  TreeRank = 0
  shape: bbox 0.64 x 10 x 4.8 mm, 18 faces (baked)
FEATURE [Part::Compound2] Compound007  label="Header_L4_10x4.8 v6"
  Links = -> [Solid054,Solid055,Solid056,Solid057,Solid058,Solid059,Solid060,Solid061]
  Placement = pos=(-11.43,2.54,-2.67) rot=(0,-0.707107,0.707107;3.14159rad)
  TreeRank = 0
FEATURE [Part::Feature] Solid062
  TreeRank = 0
  shape: bbox 2.54 x 2.5 x 2.54 mm, 26 faces (baked)
FEATURE [Part::Feature] Solid063
  TreeRank = 0
  shape: bbox 0.64 x 11.6 x 0.64 mm, 14 faces (baked)
FEATURE [Part::Feature] Solid064 .. Solid068  x5 (patterned run collapsed; names and placements below)
  TreeRank = 0
  shape: bbox 2.54 x 2.5 x 2.54 mm, 26 faces (baked)
FEATURE [Part::Feature] Solid069 .. Solid073  x5 (patterned run collapsed; names and placements below)
  TreeRank = 0
  shape: bbox 0.64 x 11.6 x 0.64 mm, 14 faces (baked)
FEATURE [Part::Compound2] Compound008  label="Header_Male_2x3x11.6 v2"
  Links = -> [Solid062,Solid063,Solid064,Solid065,Solid066,Solid067,Solid068,Solid069,Solid070,Solid071,Solid072,Solid073]
  Placement = pos=(-8.636,1.27,-38.354) rot=(0,1,0;1.5708rad)
  TreeRank = 0
FEATURE [Part::Feature] Solid074
  TreeRank = 0
  shape: bbox 2.54 x 2.5 x 2.54 mm, 26 faces (baked)
FEATURE [Part::Feature] Solid075
  TreeRank = 0
  shape: bbox 0.64 x 11.6 x 0.64 mm, 14 faces (baked)
FEATURE [Part::Feature] Solid076 .. Solid094  x19 (patterned run collapsed; names and placements below)
  TreeRank = 0
  shape: bbox 2.54 x 2.5 x 2.54 mm, 26 faces (baked)
FEATURE [Part::Feature] Solid095 .. Solid113  x19 (patterned run collapsed; names and placements below)
  TreeRank = 0
  shape: bbox 0.64 x 11.6 x 0.64 mm, 14 faces (baked)
FEATURE [Part::Compound2] Compound009  label="Header_Male_1x20x11.6 v2"
  Links = -> [Solid074,Solid075,Solid076,Solid077,Solid078,Solid079,Solid080,Solid081,Solid082,Solid083,Solid084,Solid085,Solid086,Solid087,Solid088,Solid089,Solid090,Solid091,Solid092,Solid093,Solid094,Solid095,Solid096,Solid097,Solid098,Solid099,Solid100,Solid101,Solid102,Solid103,Solid104,Solid105,Solid106,Solid107,Solid108,Solid109,Solid110,Solid111,Solid112,Solid113]
  TreeRank = 0
FEATURE [App::Link] Link  label="Header_Male_1x20x11.6 v003"
  AutoLinkLabel = false
  AutoPlacement = true
  ElementCount = 2
  LinkedObject = -> Compound009
  PlacementList = 2 placements: [(-3.81,2.22045e-15,-26.67),(-19.05,2.22045e-15,-26.67)]
  ScaleList = (2) [(1,1,1),(1,1,1)]
  ShowElement = false
  SyncGroupVisibility = false
  TreeRank = 0
  _LinkVersion = 1
FEATURE [App::Part] Part002  label="U1_STM32F103C8T6_Blue_Pill v6_a20226da84fa"
  ClaimAllChildren = false
  ExportMode = 1
  Group = -> [Solid046,Solid047,Compound006,Solid051,Solid052,Solid053,Compound007,Compound008,Link,Solid048,Solid050,Solid049,Solid054,Solid056,Solid058,Solid055,Solid059,Solid060,Solid061,Solid057,Solid068,Solid073,Solid069,Solid067,Solid071,Solid070,Solid066,Solid072,Solid063,Solid064,Solid065,Solid062]
  Origin = -> Origin010
  Placement = pos=(-11.43,-20.6775,-2.8) rot=(0,-0.707107,0.707107;3.14159rad)
  TreeRank = 0
  _ExportChildren = -> [Solid046,Solid047,Compound006,Solid051,Solid052,Solid053,Compound007,Compound008,Link]
  _GroupVersion = 1
FEATURE [App::Part] Bot_61fa
  ClaimAllChildren = false
  ExportMode = 1
  Group = -> [Part002]
  Origin = -> Origin004
  Placement = pos=(0,0,-1) rot=(0,0,1;0rad)
  TreeRank = 0
  _ExportChildren = -> [Part002]
  _GroupVersion = 1
FEATURE [App::DocumentObjectGroup] Group  label="Potentiometers"
  ClaimAllChildren = true
  ExportMode = 1
  Group = -> [Part001,VR3_B10K_B103_sliding_potentiometer_v8_0e7ca3619782_ln_,VR3_B10K_B103_sliding_potentiometer_v8_0e7ca3619782_ln_001]
  TreeRank = 1
  _GroupVersion = 1
FEATURE [App::DocumentObjectGroup] Group001  label="Encoders"
  ClaimAllChildren = true
  ExportMode = 1
  Group = -> [EN4_PEC11_4220F_S0024_05183b338953_ln_005,Shape,EN4_PEC11_4220F_S0024_05183b338953_ln_,EN4_PEC11_4220F_S0024_05183b338953_ln_001,EN4_PEC11_4220F_S0024_05183b338953_ln_002,EN4_PEC11_4220F_S0024_05183b338953_ln_003,EN4_PEC11_4220F_S0024_05183b338953_ln_004,EN4_PEC11_4220F_S0024_05183b338953_ln_006,EN4_PEC11_4220F_S0024_05183b338953_ln_007]
  TreeRank = 2
  _GroupVersion = 1
FEATURE [App::DocumentObjectGroup] Group002  label="Keycaps"
  ClaimAllChildren = true
  ExportMode = 1
  Group = -> [SW4_Keycap_adjusted_v39_b31d9dcab5e3_2__ln_004,SW4_Keycap_adjusted_v39_b31d9dcab5e3_2__ln_,SW4_Keycap_adjusted_v39_b31d9dcab5e3_2__ln_010,SW4_Keycap_adjusted_v39_b31d9dcab5e3_2__ln_003,SW4_Keycap_adjusted_v39_b31d9dcab5e3_2__ln_007,SW4_Keycap_adjusted_v39_b31d9dcab5e3_2__ln_006,SW4_Keycap_adjusted_v39_b31d9dcab5e3_2__ln_011,SW4_Keycap_adjusted_v39_b31d9dcab5e3_2__ln_009,Shape002,+6 more]
  TreeRank = 7
  _GroupVersion = 1
FEATURE [App::Part] Top_61fa
  ClaimAllChildren = false
  ExportMode = 1
  Group = -> [Shape,Compound,Solid004,Solid002,Solid,Solid003,Solid001,EN4_PEC11_4220F_S0024_05183b338953_ln_,Shape001,Shape002,D11_LED_SK6812MINI_E_v1_98239feeca95_ln_,SW4_cherry_mx_v1_b31d9dcab5e3_ln_,SW4_Keycap_adjusted_v39_b31d9dcab5e3_2__ln_,EN4_PEC11_4220F_S0024_05183b338953_ln_001,D11_LED_SK6812MINI_E_v1_98239feeca95_ln_001,EN4_PEC11_4220F_S0024_05183b338953_ln_002,+50 more]
  Origin = -> Origin003
  Placement = pos=(0,0,1.1) rot=(0,0,1;0rad)
  TreeRank = 0
  _ExportChildren = -> [Compound,Shape001,D11_LED_SK6812MINI_E_v1_98239feeca95_ln_,SW4_cherry_mx_v1_b31d9dcab5e3_ln_,D11_LED_SK6812MINI_E_v1_98239feeca95_ln_001,D11_LED_SK6812MINI_E_v1_98239feeca95_ln_002,SW4_cherry_mx_v1_b31d9dcab5e3_ln_001,D11_LED_SK6812MINI_E_v1_98239feeca95_ln_003,SW4_cherry_mx_v1_b31d9dcab5e3_ln_002,Part,D11_LED_SK6812MINI_E_v1_98239feeca95_ln_004,D11_LED_SK6812MINI_E_v1_98239feeca95_ln_005,+22 more]
  _GroupVersion = 1
FEATURE [App::Part] Step_Models_61fa
  ClaimAllChildren = false
  ExportMode = 1
  Group = -> [Top_61fa,Bot_61fa]
  Origin = -> Origin002
  TreeRank = 0
  _ExportChildren = -> [Top_61fa,Bot_61fa]
  _GroupVersion = 1
FEATURE [App::Part] Board_61fa  label="keeby cat"
  ClaimAllChildren = false
  ExportMode = 1
  Group = -> [Board_Geoms_61fa,Step_Models_61fa]
  Origin = -> Origin001
  TreeRank = 6
  _ExportChildren = -> [Board_Geoms_61fa,Step_Models_61fa]
  _GroupVersion = 1
